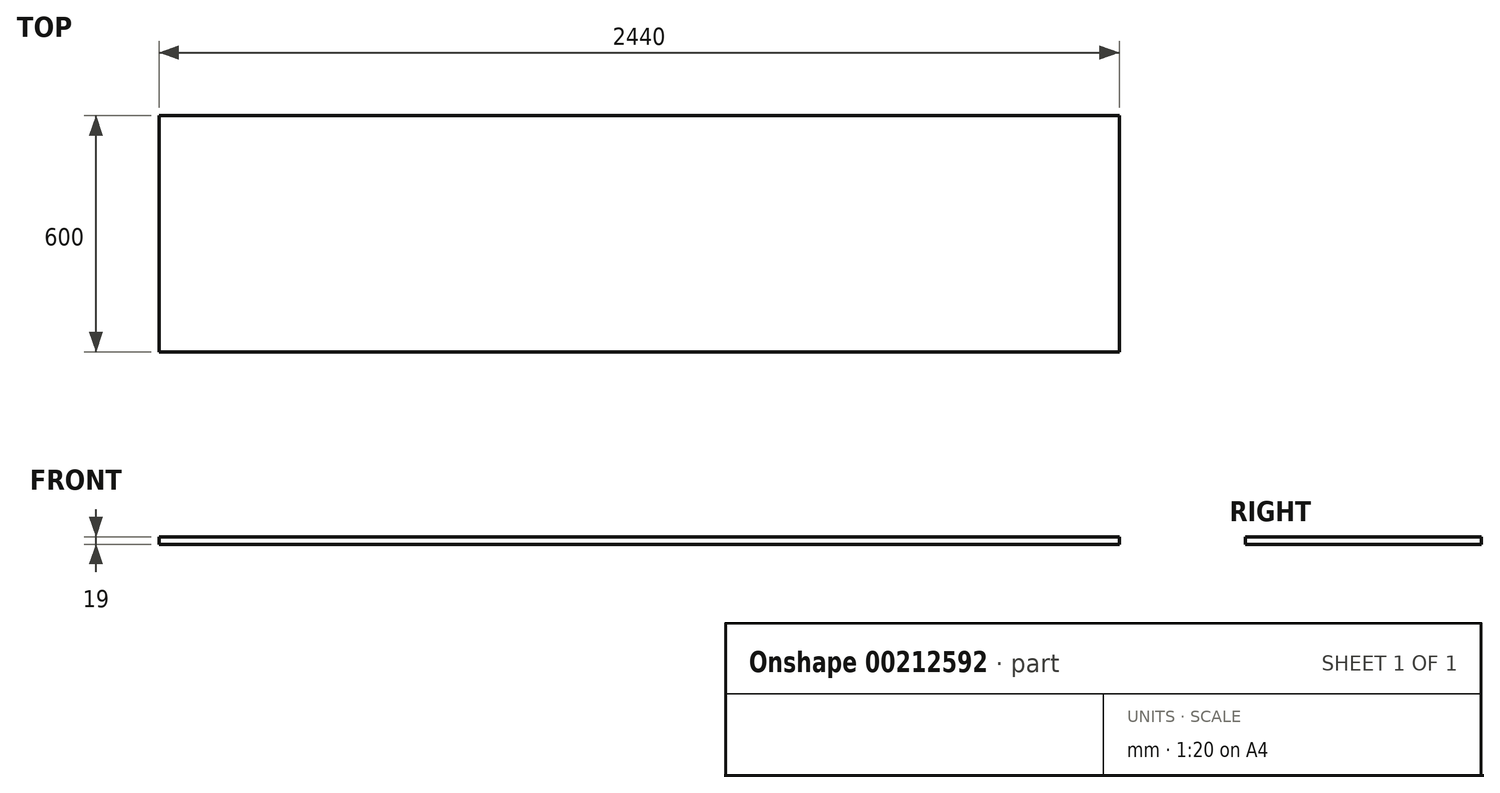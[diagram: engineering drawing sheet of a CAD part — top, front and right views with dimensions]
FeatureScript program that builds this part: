
annotation { "Feature Type Name" : "Feature", "Feature Type Description" : "" }
export const myFeature = defineFeature(function(context is Context, id is Id, definition is map)
    precondition{}
    {
        {
            var Q0;
            Q0=qCreatedBy(makeId("Top.planeOp"),FACE);
            var sketch = newSketch(context, id + "F0", { "sketchPlane" : qUnion([Q0])});
            skLineSegment(sketch, "E0.bottom", {"start": v(-1220, -300) * mm, "end": v(1220, -300) * mm});
            skLineSegment(sketch, "E0.top", {"start": v(-1220, 300) * mm, "end": v(1220, 300) * mm});
            skLineSegment(sketch, "E0.left", {"start": v(-1220, -300) * mm, "end": v(-1220, 300) * mm});
            skLineSegment(sketch, "E0.right", {"start": v(1220, -300) * mm, "end": v(1220, 300) * mm});
            skSolve(sketch);
        }
        {
            var Q0;
            Q0 = qSketchRegion(id + "F0", true);
            extrude(context, id + "F1", {"entities" : qUnion([Q0]), "depth" : 19 * mm});
        }
    });
